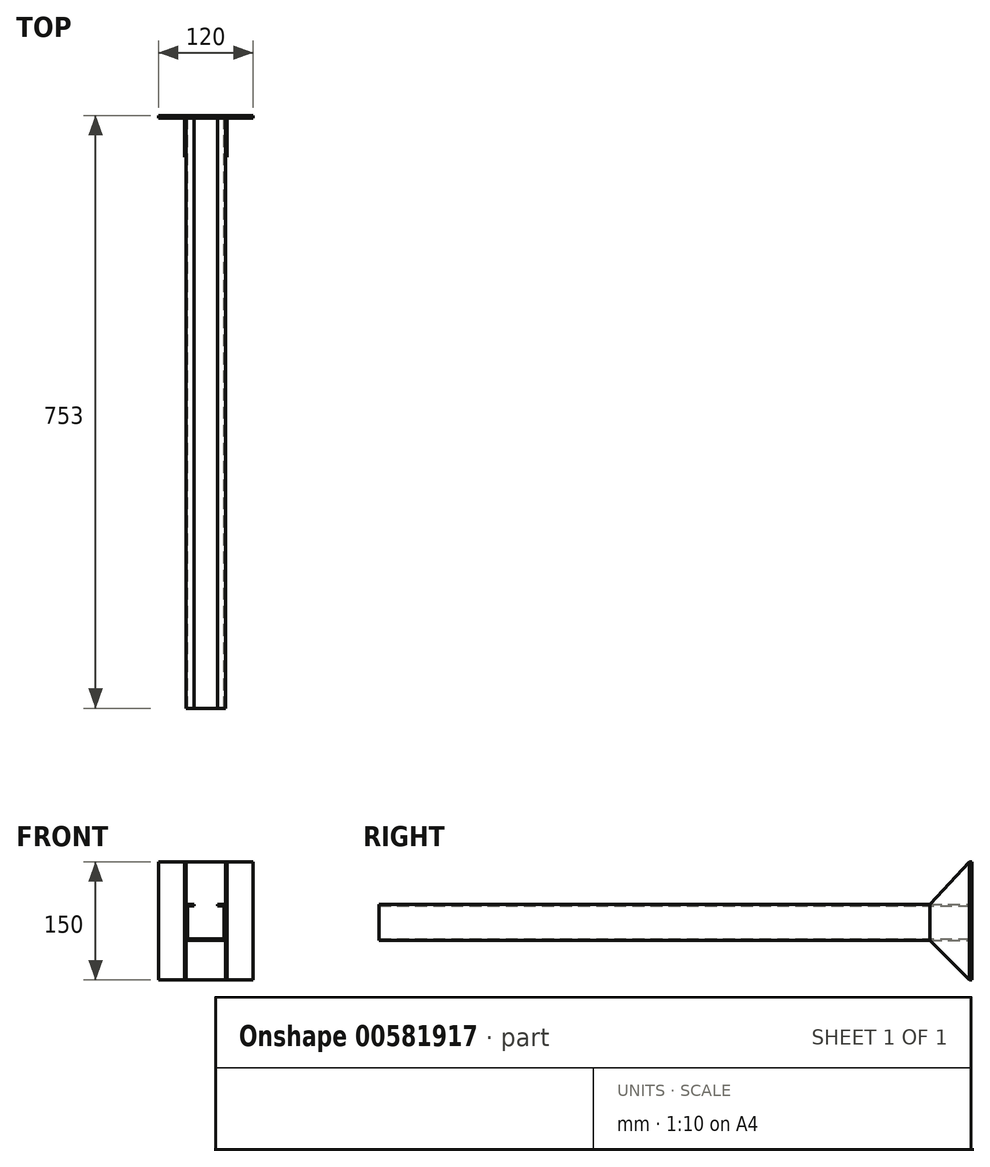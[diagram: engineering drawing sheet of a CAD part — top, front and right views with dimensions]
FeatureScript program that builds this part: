
annotation { "Feature Type Name" : "Feature", "Feature Type Description" : "" }
export const myFeature = defineFeature(function(context is Context, id is Id, definition is map)
    precondition{}
    {
        {
            var Q0;
            Q0=qCreatedBy(makeId("Front.planeOp"),FACE);
            var sketch = newSketch(context, id + "F0", { "sketchPlane" : qUnion([Q0])});
            skLineSegment(sketch, "E0.bottom", {"start": v(60, -75) * mm, "end": v(-60, -75) * mm});
            skLineSegment(sketch, "E0.top", {"start": v(60, 75) * mm, "end": v(-60, 75) * mm});
            skLineSegment(sketch, "E0.left", {"start": v(60, -75) * mm, "end": v(60, 75) * mm});
            skLineSegment(sketch, "E0.right", {"start": v(-60, -75) * mm, "end": v(-60, 75) * mm});
            skPoint(sketch, "E0.middle", {"position": v(0, 0) * mm});
            skSolve(sketch);
        }
        {
            var Q0;
            Q0=qSketchRegion(id+"F0",true);
            extrude(context, id + "F1", {"entities" : qUnion([Q0]), "oppositeDirection" : true, "depth" : 3 * mm, "offsetDistance" : 25 * mm});
        }
        {
            var Q0;
            Q0=makeQuery(id+"F1.opExtrude","CAP_FACE",FACE,{"disambiguationData":[OSD([sQuery(id+"F0.wireOp",EDGE,"E0.bottom"),sQuery(id+"F0.wireOp",EDGE,"E0.top"),sQuery(id+"F0.wireOp",EDGE,"E0.left"),sQuery(id+"F0.wireOp",EDGE,"E0.right")])],"isStart":true});
            var sketch = newSketch(context, id + "F2", { "sketchPlane" : qUnion([Q0])});
            skLineSegment(sketch, "E1", {"start": v(-15, 19.26) * mm, "end": v(-23, 19.26) * mm});
            skLineSegment(sketch, "E2", {"start": v(-23, 19.26) * mm, "end": v(-23, -23) * mm});
            skLineSegment(sketch, "E3", {"start": v(-23, -23) * mm, "end": v(23, -23) * mm});
            skLineSegment(sketch, "E4", {"start": v(23, -23) * mm, "end": v(23, 19.26) * mm});
            skLineSegment(sketch, "E5", {"start": v(23, 19.26) * mm, "end": v(15, 19.26) * mm});
            skLineSegment(sketch, "E6", {"start": v(15, 19.26) * mm, "end": v(15, 21.26) * mm});
            skLineSegment(sketch, "E7", {"start": v(15, 21.26) * mm, "end": v(25, 21.26) * mm});
            skLineSegment(sketch, "E8", {"start": v(25, 21.26) * mm, "end": v(25, -25) * mm});
            skLineSegment(sketch, "E9", {"start": v(25, -25) * mm, "end": v(-25, -25) * mm});
            skLineSegment(sketch, "E10", {"start": v(-25, -25) * mm, "end": v(-25, 21.26) * mm});
            skLineSegment(sketch, "E11", {"start": v(-25, 21.26) * mm, "end": v(-15, 21.26) * mm});
            skLineSegment(sketch, "E12", {"start": v(-15, 21.26) * mm, "end": v(-15, 19.26) * mm});
            skSolve(sketch);
        }
        {
            var Q0;
            Q0=qSketchRegion(id+"F2",true);
            extrude(context, id + "F3", {"entities" : qUnion([Q0]), "operationType" : NewBodyOperationType.ADD, "depth" : 750 * mm, "offsetDistance" : 25 * mm});
        }
        {
            var Q0;
            Q0=makeQuery(id+"F3.opExtrude","SWEPT_FACE",FACE,{"disambiguationData":[OSD([sQuery(id+"F2.wireOp",EDGE,"E8")])]});
            var sketch = newSketch(context, id + "F4", { "sketchPlane" : qUnion([Q0])});
            skLineSegment(sketch, "E13.0", {"start": v(0, -75) * mm, "end": v(0, 75) * mm});
            skLineSegment(sketch, "E14", {"start": v(0, 75) * mm, "end": v(-50, 21.26) * mm});
            skLineSegment(sketch, "E15", {"start": v(-50, 21.26) * mm, "end": v(-50, -25) * mm});
            skLineSegment(sketch, "E16", {"start": v(-50, -25) * mm, "end": v(0, -75) * mm});
            skSolve(sketch);
        }
        {
            var Q0;
            Q0=qSketchRegion(id+"F4",true);
            extrude(context, id + "F5", {"entities" : qUnion([Q0]), "operationType" : NewBodyOperationType.ADD, "depth" : 2 * mm, "offsetDistance" : 25 * mm});
        }
        {
            var Q0;
            Q0=makeQuery(id+"F3.opExtrude","SWEPT_FACE",FACE,{"disambiguationData":[OSD([sQuery(id+"F2.wireOp",EDGE,"E10")])]});
            var sketch = newSketch(context, id + "F6", { "sketchPlane" : qUnion([Q0])});
            skLineSegment(sketch, "E17.0", {"start": v(0, -75) * mm, "end": v(0, 75) * mm});
            skLineSegment(sketch, "E18", {"start": v(0, 75) * mm, "end": v(50, 21.26) * mm});
            skLineSegment(sketch, "E19", {"start": v(50, 21.26) * mm, "end": v(50, -25) * mm});
            skLineSegment(sketch, "E20", {"start": v(50, -25) * mm, "end": v(0, -75) * mm});
            skSolve(sketch);
        }
        {
            var Q0;
            Q0=qSketchRegion(id+"F6",true);
            extrude(context, id + "F7", {"entities" : qUnion([Q0]), "operationType" : NewBodyOperationType.ADD, "depth" : 2 * mm, "offsetDistance" : 25 * mm});
        }
    });
